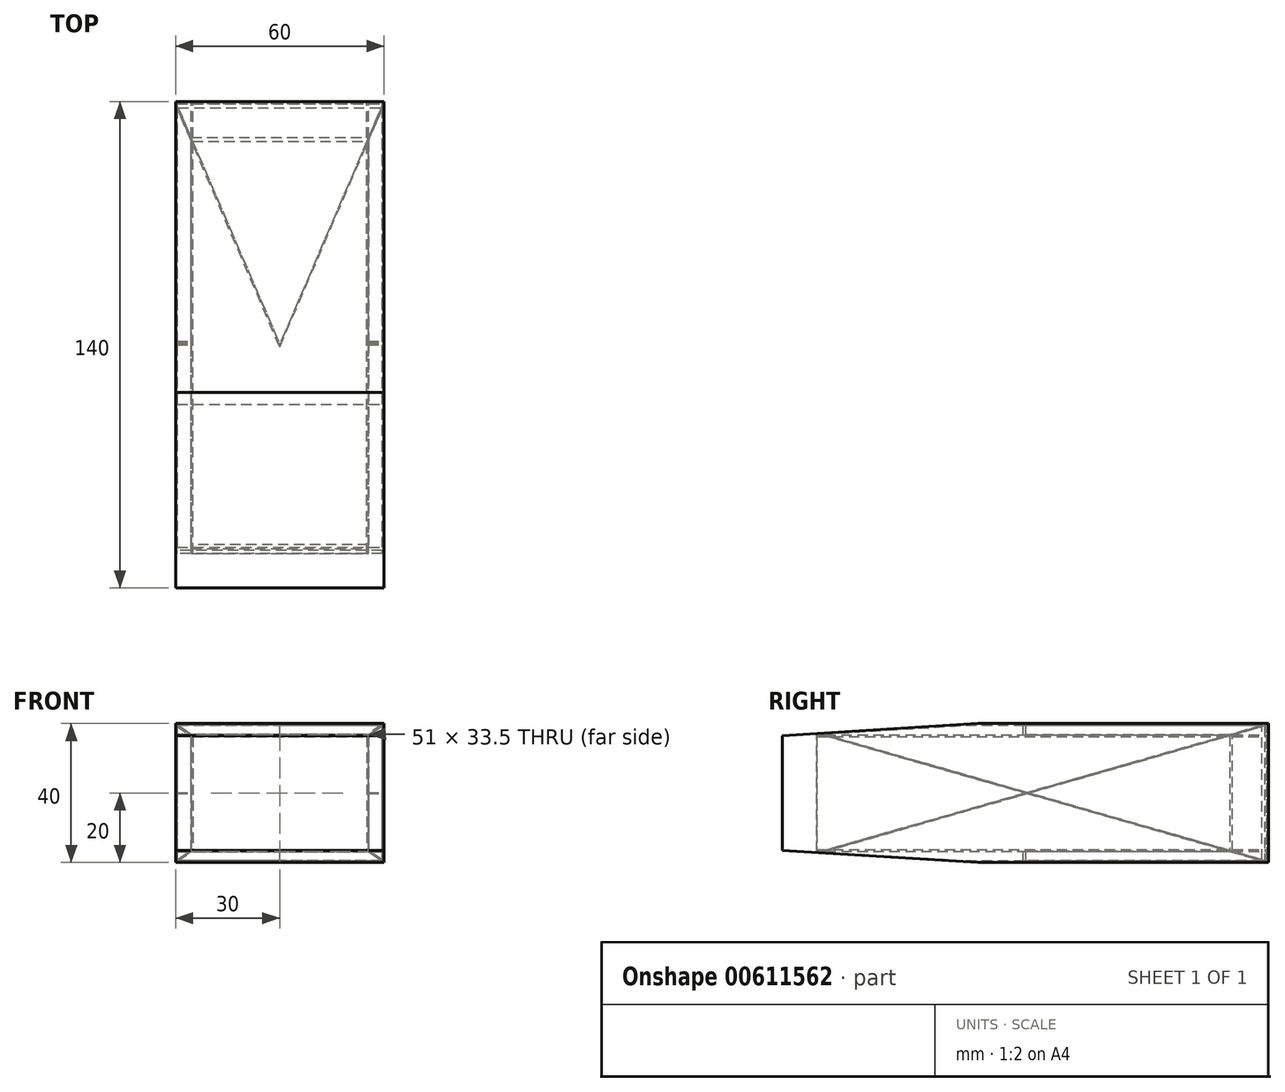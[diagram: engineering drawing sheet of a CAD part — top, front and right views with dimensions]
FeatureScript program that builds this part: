
annotation { "Feature Type Name" : "Feature", "Feature Type Description" : "" }
export const myFeature = defineFeature(function(context is Context, id is Id, definition is map)
    precondition{}
    {
        {
            var Q0;
            Q0=qCreatedBy(makeId("Front.planeOp"),FACE);
            var sketch = newSketch(context, id + "F0", { "sketchPlane" : qUnion([Q0])});
            skLineSegment(sketch, "E0.bottom", {"start": v(-30, -20) * mm, "end": v(30, -20) * mm});
            skLineSegment(sketch, "E0.top", {"start": v(-30, 20) * mm, "end": v(30, 20) * mm});
            skLineSegment(sketch, "E0.left", {"start": v(-30, -20) * mm, "end": v(-30, 20) * mm});
            skLineSegment(sketch, "E0.right", {"start": v(30, -20) * mm, "end": v(30, 20) * mm});
            skPoint(sketch, "E0.middle", {"position": v(0, 0) * mm});
            skLineSegment(sketch, "E1.bottom", {"start": v(-25, 16.25) * mm, "end": v(25, 16.25) * mm});
            skLineSegment(sketch, "E1.top", {"start": v(-25, -16.25) * mm, "end": v(25, -16.25) * mm});
            skLineSegment(sketch, "E1.left", {"start": v(-25, 16.25) * mm, "end": v(-25, -16.25) * mm});
            skLineSegment(sketch, "E1.right", {"start": v(25, 16.25) * mm, "end": v(25, -16.25) * mm});
            skSolve(sketch);
        }
        {
            var Q0;
            Q0=qSketchRegion(id+"F0",true);
            extrude(context, id + "F1", {"entities" : qUnion([Q0]), "depth" : 140 * mm, "offsetDistance" : 25 * mm});
        }
        {
            var Q0;
            Q0=makeQuery(id+"F1.opExtrude","CAP_FACE",FACE,{"disambiguationData":[OSD([sQuery(id+"F0.wireOp",EDGE,"E0.bottom"),sQuery(id+"F0.wireOp",EDGE,"E0.top"),sQuery(id+"F0.wireOp",EDGE,"E0.left"),sQuery(id+"F0.wireOp",EDGE,"E0.right")])],"isStart":false});
            var Q1;
            Q1=makeQuery(id+"F1.opExtrude","SWEPT_BODY",BODY,{"disambiguationData":[OSD([sQuery(id+"F0.wireOp",EDGE,"E0.bottom"),sQuery(id+"F0.wireOp",EDGE,"E0.top"),sQuery(id+"F0.wireOp",EDGE,"E0.left"),sQuery(id+"F0.wireOp",EDGE,"E0.right"),sQuery(id+"F0.wireOp",EDGE,"E1.bottom"),sQuery(id+"F0.wireOp",EDGE,"E1.top"),sQuery(id+"F0.wireOp",EDGE,"E1.left"),sQuery(id+"F0.wireOp",EDGE,"E1.right")])]});
            shell(context, id + "F2", {"isHollow" : true, "entities" : qUnion([Q0]), "parts" : qUnion([Q1]), "thickness" : 0.5 * mm});
        }
        {
            var Q0;
            Q0=makeQuery(id+"F1.opExtrude","SWEPT_FACE",FACE,{"disambiguationData":[OSD([sQuery(id+"F0.wireOp",EDGE,"E0.top")])]});
            var sketch = newSketch(context, id + "F3", { "sketchPlane" : qUnion([Q0])});
            skLineSegment(sketch, "E2", {"start": v(30, -26.97) * mm, "end": v(30, -27.3) * mm});
            skLineSegment(sketch, "E3", {"start": v(-30, 0) * mm, "end": v(-30, -0.32) * mm});
            skLineSegment(sketch, "E4", {"start": v(-30, 0) * mm, "end": v(30, -139.71) * mm});
            skLineSegment(sketch, "E5", {"start": v(30, -139.71) * mm, "end": v(30, -140.44) * mm});
            skLineSegment(sketch, "E6", {"start": v(30, -140.44) * mm, "end": v(-30, -0.73) * mm});
            skLineSegment(sketch, "E7", {"start": v(30, -140) * mm, "end": v(30, -139.71) * mm});
            skLineSegment(sketch, "E8.0.0", {"start": v(29.5, -0.5) * mm, "end": v(-29.5, -0.5) * mm});
            skLineSegment(sketch, "E8.0.2", {"start": v(-29.5, -0.5) * mm, "end": v(29.5, -0.5) * mm});
            skLineSegment(sketch, "E9.MirrorCS", {"start": v(-30, -140.44) * mm, "end": v(30, -0.73) * mm});
            skLineSegment(sketch, "E10.MirrorCS", {"start": v(30, 0) * mm, "end": v(-30, -139.71) * mm});
            skLineSegment(sketch, "E11", {"start": v(-0.32, 0) * mm, "end": v(0.32, 0) * mm});
            skLineSegment(sketch, "E12", {"start": v(30, -69.26) * mm, "end": v(30, -70.73) * mm});
            skLineSegment(sketch, "E13", {"start": v(-30, -69.26) * mm, "end": v(-30, -70.73) * mm});
            skLineSegment(sketch, "E14", {"start": v(-30, -0.73) * mm, "end": v(-30, 0) * mm});
            skLineSegment(sketch, "E15", {"start": v(30, 0) * mm, "end": v(30, -0.73) * mm});
            skLineSegment(sketch, "E16", {"start": v(-30, -140.44) * mm, "end": v(-30, -139.71) * mm});
            skLineSegment(sketch, "E17", {"start": v(-0.25, -140) * mm, "end": v(0.25, -140) * mm});
            skLineSegment(sketch, "E18", {"start": v(30, -140) * mm, "end": v(29.8, -140) * mm});
            skLineSegment(sketch, "E19", {"start": v(-30, -139.71) * mm, "end": v(-30, -140) * mm});
            skLineSegment(sketch, "E20", {"start": v(-30, -140) * mm, "end": v(-29.8, -140) * mm});
            skSolve(sketch);
        }
        {
            var Q0;
            {var subQ0=sQuery(id+"F3.wireOp",EDGE,"E19");Q0=makeQuery(id+"F3.imprint","IMPRINT",FACE,{"disambiguationData":[TD([[makeQuery(id+"F3.imprint","IMPRINT",EDGE,{"derivedFrom":subQ0}),-1.0]])]});}
            var Q1;
            {var subQ5=sQuery(id+"F3.wireOp",EDGE,"E7");Q1=makeQuery(id+"F3.imprint","IMPRINT",FACE,{"disambiguationData":[TD([[makeQuery(id+"F3.imprint","IMPRINT",EDGE,{"derivedFrom":subQ5}),1.0]])]});}
            var Q2;
            {var subQ1=sQuery(id+"F3.wireOp",EDGE,"E4");var subQ4=sQuery(id+"F3.wireOp",EDGE,"E10.MirrorCS");var subQ5=makeQuery(id+"F3.imprint","INTERSECT",VERTEX,{"derivedFrom":[subQ1,subQ4]});Q2=makeQuery(id+"F3.imprint","IMPRINT",FACE,{"disambiguationData":[TD([[makeQuery(id+"F3.imprint","IMPRINT",EDGE,{"disambiguationData":[TD([[subQ5,-1.0]])],"derivedFrom":subQ4}),-1.0]])]});}
            var Q3;
            {var subQ0=sQuery(id+"F3.wireOp",EDGE,"E10.MirrorCS");var subQ1=sQuery(id+"F3.wireOp",EDGE,"E4");var subQ2=makeQuery(id+"F3.imprint","INTERSECT",VERTEX,{"derivedFrom":[subQ1,subQ0]});Q3=makeQuery(id+"F3.imprint","IMPRINT",FACE,{"disambiguationData":[TD([[makeQuery(id+"F3.imprint","IMPRINT",EDGE,{"disambiguationData":[TD([[subQ2,-1.0]])],"derivedFrom":subQ1}),-1.0]])]});}
            var Q4;
            {var subQ5=sQuery(id+"F3.wireOp",EDGE,"E15");Q4=makeQuery(id+"F3.imprint","IMPRINT",FACE,{"disambiguationData":[TD([[makeQuery(id+"F3.imprint","IMPRINT",EDGE,{"derivedFrom":subQ5}),1.0]])]});}
            var Q5;
            Q5=makeQuery(id+"F1.opExtrude","SWEPT_FACE",FACE,{"disambiguationData":[OSD([sQuery(id+"F0.wireOp",EDGE,"E0.bottom")])]});
            extrude(context, id + "F4", {"entities" : qUnion([Q0, Q1, Q2, Q3, Q4]), "operationType" : NewBodyOperationType.ADD, "endBound" : BoundingType.UP_TO_SURFACE, "oppositeDirection" : true, "depth" : 25 * mm, "endBoundEntityFace" : qUnion([Q5]), "offsetDistance" : 25 * mm});
        }
        {
            var Q0;
            Q0=makeQuery(id+"F1.opExtrude","SWEPT_FACE",FACE,{"disambiguationData":[OSD([sQuery(id+"F0.wireOp",EDGE,"E0.right")])]});
            var sketch = newSketch(context, id + "F5", { "sketchPlane" : qUnion([Q0])});
            skLineSegment(sketch, "E21", {"start": v(-140, -20) * mm, "end": v(0, 20) * mm});
            skLineSegment(sketch, "E22", {"start": v(0, 20) * mm, "end": v(0, 19.7) * mm});
            skLineSegment(sketch, "E23", {"start": v(0, 19.7) * mm, "end": v(-138.94, -20) * mm});
            skLineSegment(sketch, "E24", {"start": v(-140, 20) * mm, "end": v(0, -20) * mm});
            skLineSegment(sketch, "E25", {"start": v(0, -20) * mm, "end": v(0, -19.7) * mm});
            skLineSegment(sketch, "E26", {"start": v(0, -19.7) * mm, "end": v(-138.94, 20) * mm});
            skSolve(sketch);
        }
        {
            var Q0;
            Q0=qSketchRegion(id+"F5",true);
            var Q1;
            {var subQ0=sQuery(id+"F5.wireOp",EDGE,"E24");var subQ1=sQuery(id+"F5.wireOp",EDGE,"E21");var subQ2=makeQuery(id+"F5.imprint","INTERSECT",VERTEX,{"derivedFrom":[subQ1,subQ0]});Q1=makeQuery(id+"F5.imprint","IMPRINT",FACE,{"disambiguationData":[TD([[makeQuery(id+"F5.imprint","IMPRINT",EDGE,{"disambiguationData":[TD([[subQ2,-1.0]])],"derivedFrom":subQ1}),1.0]])]});}
            var Q2;
            {var subQ0=sQuery(id+"F5.wireOp",EDGE,"E21");var subQ4=sQuery(id+"F5.wireOp",EDGE,"E24");var subQ5=makeQuery(id+"F5.imprint","INTERSECT",VERTEX,{"derivedFrom":[subQ0,subQ4]});Q2=makeQuery(id+"F5.imprint","IMPRINT",FACE,{"disambiguationData":[TD([[makeQuery(id+"F5.imprint","IMPRINT",EDGE,{"disambiguationData":[TD([[subQ5,-1.0]])],"derivedFrom":subQ4}),-1.0]])]});}
            var Q3;
            Q3=makeQuery(id+"F1.opExtrude","SWEPT_FACE",FACE,{"disambiguationData":[OSD([sQuery(id+"F0.wireOp",EDGE,"E0.left")])]});
            extrude(context, id + "F6", {"entities" : qUnion([Q0, Q1, Q2]), "operationType" : NewBodyOperationType.ADD, "endBound" : BoundingType.UP_TO_SURFACE, "oppositeDirection" : true, "depth" : 25 * mm, "endBoundEntityFace" : qUnion([Q3]), "offsetDistance" : 25 * mm});
        }
        {
            var Q0;
            Q0=makeQuery(id+"F0.imprint","IMPRINT",FACE,{"disambiguationData":[TD([[makeQuery(id+"F0.imprint","IMPRINT",EDGE,{"derivedFrom":sQuery(id+"F0.wireOp",EDGE,"E1.bottom")}),-1.0]])]});
            extrude(context, id + "F7", {"entities" : qUnion([Q0]), "operationType" : NewBodyOperationType.REMOVE, "depth" : 140 * mm, "offsetDistance" : 25 * mm});
        }
        {
            var Q0;
            Q0=makeQuery(id+"F1.opExtrude","SWEPT_FACE",FACE,{"disambiguationData":[OSD([sQuery(id+"F0.wireOp",EDGE,"E0.right")])]});
            var sketch = newSketch(context, id + "F8", { "sketchPlane" : qUnion([Q0])});
            skLineSegment(sketch, "E27", {"start": v(-140, 20) * mm, "end": v(-130, 20) * mm});
            skLineSegment(sketch, "E28", {"start": v(-130, 20) * mm, "end": v(-130, -20) * mm});
            skSolve(sketch);
        }
        {
            var Q0;
            Q0 = qSketchRegion(id + "F8", true);
            var Q1;
            Q1=makeQuery(id+"F8.imprint","IMPRINT",FACE,{"disambiguationData":[TD([[makeQuery(id+"F8.imprint","IMPRINT",EDGE,{"derivedFrom":sQuery(id+"F8.wireOp",EDGE,"E27")}),-1.0]])]});
            var Q2;
            Q2=makeQuery(id+"F1.opExtrude","SWEPT_FACE",FACE,{"disambiguationData":[OSD([sQuery(id+"F0.wireOp",EDGE,"E0.left")])]});
            extrude(context, id + "F9", {"entities" : qUnion([Q0, Q1]), "operationType" : NewBodyOperationType.ADD, "endBound" : BoundingType.UP_TO_SURFACE, "oppositeDirection" : true, "depth" : 25 * mm, "endBoundEntityFace" : qUnion([Q2]), "offsetDistance" : 25 * mm});
        }
        {
            var Q0;
            Q0=makeQuery(id+"F1.opExtrude","SWEPT_FACE",FACE,{"disambiguationData":[OSD([sQuery(id+"F0.wireOp",EDGE,"E0.left")])]});
            var sketch = newSketch(context, id + "F10", { "sketchPlane" : qUnion([Q0])});
            skLineSegment(sketch, "E29", {"start": v(140, -20) * mm, "end": v(140, -16.25) * mm});
            skLineSegment(sketch, "E30", {"start": v(140, -16.25) * mm, "end": v(78.96, -20) * mm});
            skLineSegment(sketch, "E31", {"start": v(140, -16.25) * mm, "end": v(140, -16.54) * mm});
            skLineSegment(sketch, "E32", {"start": v(140, -16.54) * mm, "end": v(83.68, -20) * mm});
            skLineSegment(sketch, "E33.MirrorCS", {"start": v(140, 16.54) * mm, "end": v(83.68, 20) * mm});
            skLineSegment(sketch, "E34.MirrorCS", {"start": v(140, 16.25) * mm, "end": v(78.96, 20) * mm});
            skSolve(sketch);
        }
        {
            var Q0;
            {var subQ0=sQuery(id+"F10.wireOp",EDGE,"E29");Q0=makeQuery(id+"F10.imprint","IMPRINT",FACE,{"disambiguationData":[TD([[makeQuery(id+"F10.imprint","IMPRINT",EDGE,{"derivedFrom":subQ0}),1.0]])]});}
            var Q1;
            {var subQ0=sQuery(id+"F10.wireOp",EDGE,"E33.MirrorCS");Q1=makeQuery(id+"F10.imprint","IMPRINT",FACE,{"disambiguationData":[TD([[makeQuery(id+"F10.imprint","IMPRINT",EDGE,{"derivedFrom":subQ0}),-1.0]])]});}
            var Q2;
            Q2=makeQuery(id+"F1.opExtrude","SWEPT_FACE",FACE,{"disambiguationData":[OSD([sQuery(id+"F0.wireOp",EDGE,"E0.right")])]});
            extrude(context, id + "F11", {"entities" : qUnion([Q0, Q1]), "operationType" : NewBodyOperationType.REMOVE, "endBound" : BoundingType.UP_TO_SURFACE, "oppositeDirection" : true, "depth" : 25 * mm, "endBoundEntityFace" : qUnion([Q2]), "offsetDistance" : 25 * mm});
        }
        {
            var Q0;
            {var subQ0=sQuery(id+"F10.wireOp",EDGE,"E33.MirrorCS");Q0=makeQuery(id+"F10.imprint","IMPRINT",FACE,{"disambiguationData":[TD([[makeQuery(id+"F10.imprint","IMPRINT",EDGE,{"derivedFrom":subQ0}),1.0]])]});}
            var Q1;
            {var subQ0=sQuery(id+"F10.wireOp",EDGE,"E30");Q1=makeQuery(id+"F10.imprint","IMPRINT",FACE,{"disambiguationData":[TD([[makeQuery(id+"F10.imprint","IMPRINT",EDGE,{"derivedFrom":subQ0}),1.0]])]});}
            var Q2;
            Q2=makeQuery(id+"F1.opExtrude","SWEPT_FACE",FACE,{"disambiguationData":[OSD([sQuery(id+"F0.wireOp",EDGE,"E0.right")])]});
            extrude(context, id + "F12", {"entities" : qUnion([Q0, Q1]), "operationType" : NewBodyOperationType.ADD, "endBound" : BoundingType.UP_TO_SURFACE, "oppositeDirection" : true, "depth" : 25 * mm, "endBoundEntityFace" : qUnion([Q2]), "offsetDistance" : 25 * mm});
        }
    });
